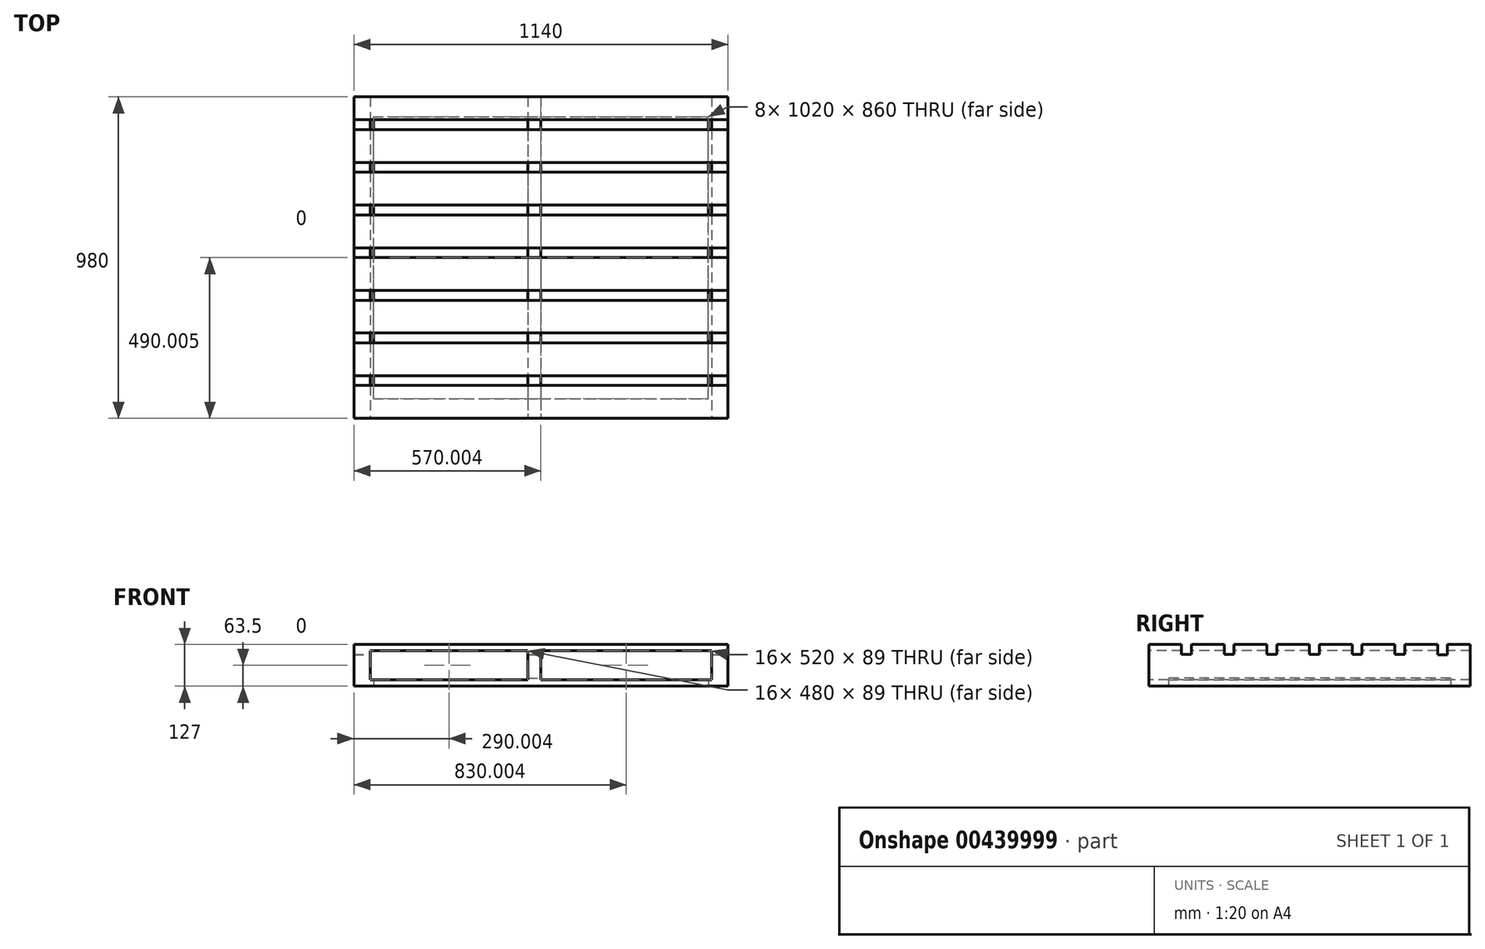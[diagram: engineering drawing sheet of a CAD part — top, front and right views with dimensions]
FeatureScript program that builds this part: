
annotation { "Feature Type Name" : "Feature", "Feature Type Description" : "" }
export const myFeature = defineFeature(function(context is Context, id is Id, definition is map)
    precondition{}
    {
        {
            var Q0;
            Q0=qCreatedBy(makeId("Top.planeOp"),FACE);
            var sketch = newSketch(context, id + "F0", { "sketchPlane" : qUnion([Q0])});
            skLineSegment(sketch, "E0.bottom", {"start": v(-571.38, 336.13) * mm, "end": v(568.62, 336.13) * mm});
            skLineSegment(sketch, "E0.top", {"start": v(-571.38, -643.87) * mm, "end": v(568.62, -643.87) * mm});
            skLineSegment(sketch, "E0.left", {"start": v(-571.38, 336.13) * mm, "end": v(-571.38, -643.87) * mm});
            skLineSegment(sketch, "E0.right", {"start": v(568.62, 336.13) * mm, "end": v(568.62, -643.87) * mm});
            skSolve(sketch);
        }
        {
            var Q0;
            Q0 = qSketchRegion(id + "F0", true);
            extrude(context, id + "F1", {"entities" : qUnion([Q0]), "depth" : 127 * mm});
        }
        {
            var Q0;
            Q0=makeQuery(id+"F1.opExtrude","SWEPT_FACE",FACE,{"disambiguationData":[OSD([sQuery(id+"F0.wireOp",EDGE,"E0.top")])]});
            var sketch = newSketch(context, id + "F2", { "sketchPlane" : qUnion([Q0])});
            skLineSegment(sketch, "E1.bottom", {"start": v(-521.38, 108) * mm, "end": v(-41.38, 108) * mm});
            skLineSegment(sketch, "E1.top", {"start": v(-521.38, 19) * mm, "end": v(-41.38, 19) * mm});
            skLineSegment(sketch, "E1.left", {"start": v(-521.38, 108) * mm, "end": v(-521.38, 19) * mm});
            skLineSegment(sketch, "E1.right", {"start": v(518.62, 108) * mm, "end": v(518.62, 19) * mm});
            skLineSegment(sketch, "E2.left", {"start": v(-41.38, 108) * mm, "end": v(-41.38, 19) * mm});
            skLineSegment(sketch, "E2.right", {"start": v(-1.38, 108) * mm, "end": v(-1.38, 19) * mm});
            skLineSegment(sketch, "E3.trimOffspring", {"start": v(-1.38, 108) * mm, "end": v(518.62, 108) * mm});
            skLineSegment(sketch, "E4.trimOffspring", {"start": v(-1.38, 19) * mm, "end": v(518.62, 19) * mm});
            skSolve(sketch);
        }
        {
            var Q0;
            Q0 = qSketchRegion(id + "F2", true);
            extrude(context, id + "F3", {"entities" : qUnion([Q0]), "operationType" : NewBodyOperationType.REMOVE, "endBound" : BoundingType.THROUGH_ALL, "oppositeDirection" : true, "depth" : 25 * mm});
        }
        {
            var Q0;
            Q0=makeQuery(id+"F1.opExtrude","SWEPT_FACE",FACE,{"disambiguationData":[OSD([sQuery(id+"F0.wireOp",EDGE,"E0.right")])]});
            var sketch = newSketch(context, id + "F4", { "sketchPlane" : qUnion([Q0])});
            skLineSegment(sketch, "E5.left", {"start": v(-543.87, 127) * mm, "end": v(-543.87, 97) * mm});
            skLineSegment(sketch, "E5.right", {"start": v(236.13, 127) * mm, "end": v(236.13, 97) * mm});
            skLineSegment(sketch, "E6", {"start": v(-513.87, 127) * mm, "end": v(-513.87, 97) * mm});
            skLineSegment(sketch, "E7.right", {"start": v(-413.87, 127) * mm, "end": v(-413.87, 97) * mm});
            skLineSegment(sketch, "E8.right", {"start": v(-383.87, 127) * mm, "end": v(-383.87, 97) * mm});
            skLineSegment(sketch, "E9.right", {"start": v(-283.87, 127) * mm, "end": v(-283.87, 97) * mm});
            skLineSegment(sketch, "E10.right", {"start": v(-253.87, 127) * mm, "end": v(-253.87, 97) * mm});
            skLineSegment(sketch, "E11.right", {"start": v(-153.87, 127) * mm, "end": v(-153.87, 97) * mm});
            skLineSegment(sketch, "E12.right", {"start": v(-123.87, 127) * mm, "end": v(-123.87, 97) * mm});
            skLineSegment(sketch, "E13", {"start": v(-23.87, 127) * mm, "end": v(-23.87, 97) * mm});
            skLineSegment(sketch, "E14", {"start": v(6.13, 127) * mm, "end": v(6.13, 97) * mm});
            skLineSegment(sketch, "E15", {"start": v(106.13, 127) * mm, "end": v(106.13, 97) * mm});
            skLineSegment(sketch, "E16", {"start": v(136.13, 127) * mm, "end": v(136.13, 97) * mm});
            skLineSegment(sketch, "E17", {"start": v(-543.87, 127) * mm, "end": v(-513.87, 127) * mm});
            skLineSegment(sketch, "E18", {"start": v(-543.87, 97) * mm, "end": v(-513.87, 97) * mm});
            skLineSegment(sketch, "E19", {"start": v(-413.87, 97) * mm, "end": v(-383.87, 97) * mm});
            skLineSegment(sketch, "E20", {"start": v(-413.87, 127) * mm, "end": v(-383.87, 127) * mm});
            skLineSegment(sketch, "E21", {"start": v(-283.87, 127) * mm, "end": v(-253.87, 127) * mm});
            skLineSegment(sketch, "E22", {"start": v(-283.87, 97) * mm, "end": v(-253.87, 97) * mm});
            skLineSegment(sketch, "E23", {"start": v(-153.87, 127) * mm, "end": v(-123.87, 127) * mm});
            skLineSegment(sketch, "E24", {"start": v(-153.87, 97) * mm, "end": v(-123.87, 97) * mm});
            skLineSegment(sketch, "E25", {"start": v(-23.87, 127) * mm, "end": v(6.13, 127) * mm});
            skLineSegment(sketch, "E26", {"start": v(-23.87, 97) * mm, "end": v(6.13, 97) * mm});
            skLineSegment(sketch, "E27", {"start": v(106.13, 127) * mm, "end": v(136.13, 127) * mm});
            skLineSegment(sketch, "E28", {"start": v(106.13, 97) * mm, "end": v(136.13, 97) * mm});
            skLineSegment(sketch, "E29.bottom", {"start": v(236.13, 127) * mm, "end": v(266.13, 127) * mm});
            skLineSegment(sketch, "E29.top", {"start": v(236.13, 95.56) * mm, "end": v(266.13, 95.56) * mm});
            skLineSegment(sketch, "E29.left", {"start": v(236.13, 127) * mm, "end": v(236.13, 95.56) * mm});
            skLineSegment(sketch, "E29.right", {"start": v(266.13, 127) * mm, "end": v(266.13, 95.56) * mm});
            skSolve(sketch);
        }
        {
            var Q0;
            Q0 = qSketchRegion(id + "F4", true);
            extrude(context, id + "F5", {"entities" : qUnion([Q0]), "operationType" : NewBodyOperationType.REMOVE, "endBound" : BoundingType.THROUGH_ALL, "oppositeDirection" : true, "depth" : 25 * mm});
        }
        {
            var Q0;
            Q0=makeQuery(id+"F1.opExtrude","CAP_FACE",FACE,{"disambiguationData":[OSD([sQuery(id+"F0.wireOp",EDGE,"E0.bottom"),sQuery(id+"F0.wireOp",EDGE,"E0.top"),sQuery(id+"F0.wireOp",EDGE,"E0.left"),sQuery(id+"F0.wireOp",EDGE,"E0.right")])],"isStart":true});
            var sketch = newSketch(context, id + "F6", { "sketchPlane" : qUnion([Q0])});
            skLineSegment(sketch, "E30.bottom", {"start": v(-511.38, 583.87) * mm, "end": v(508.62, 583.87) * mm});
            skLineSegment(sketch, "E30.top", {"start": v(-511.38, -276.13) * mm, "end": v(508.62, -276.13) * mm});
            skLineSegment(sketch, "E30.left", {"start": v(-511.38, 583.87) * mm, "end": v(-511.38, -276.13) * mm});
            skLineSegment(sketch, "E30.right", {"start": v(508.62, 583.87) * mm, "end": v(508.62, -276.13) * mm});
            skSolve(sketch);
        }
        {
            var Q0;
            Q0 = qSketchRegion(id + "F6", true);
            extrude(context, id + "F7", {"entities" : qUnion([Q0]), "operationType" : NewBodyOperationType.REMOVE, "oppositeDirection" : true, "depth" : 25 * mm});
        }
    });
